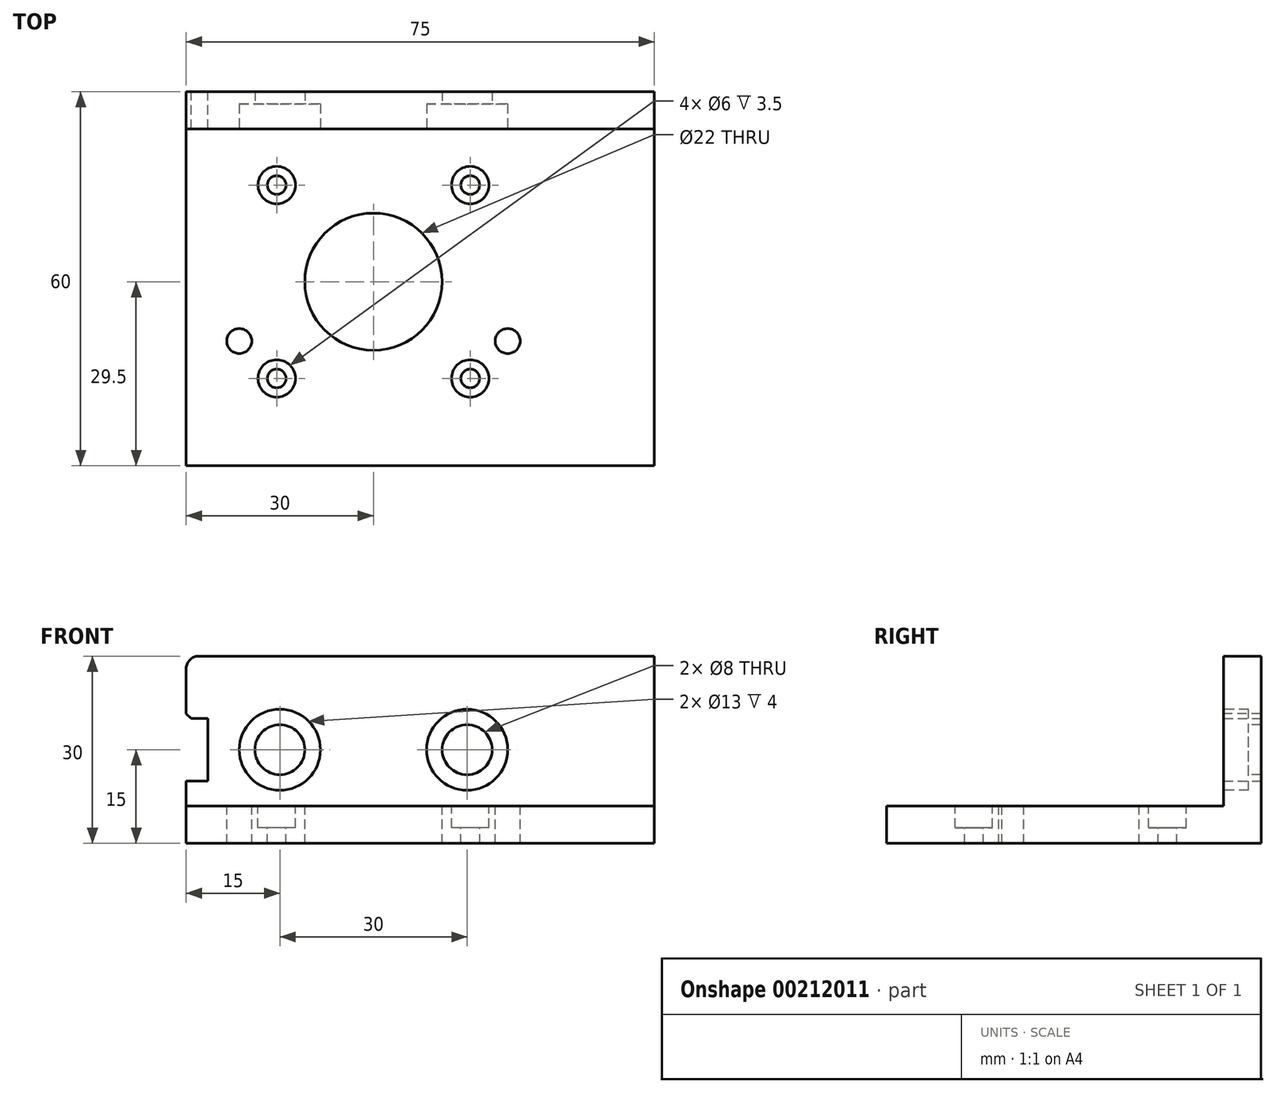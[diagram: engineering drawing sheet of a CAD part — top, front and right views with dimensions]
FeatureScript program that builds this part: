
annotation { "Feature Type Name" : "Feature", "Feature Type Description" : "" }
export const myFeature = defineFeature(function(context is Context, id is Id, definition is map)
    precondition{}
    {
        {
            var Q0;
            Q0=qCreatedBy(makeId("Top.planeOp"),FACE);
            var sketch = newSketch(context, id + "F0", { "sketchPlane" : qUnion([Q0])});
            skLineSegment(sketch, "E0.bottom", {"start": v(37.5, 30) * mm, "end": v(-37.5, 30) * mm});
            skLineSegment(sketch, "E0.top", {"start": v(37.5, -30) * mm, "end": v(-37.5, -30) * mm});
            skLineSegment(sketch, "E0.left", {"start": v(37.5, 30) * mm, "end": v(37.5, -30) * mm});
            skLineSegment(sketch, "E0.right", {"start": v(-37.5, 30) * mm, "end": v(-37.5, -30) * mm});
            skPoint(sketch, "E0.middle", {"position": v(0, 0) * mm});
            skSolve(sketch);
        }
        {
            var Q0;
            Q0 = qSketchRegion(id + "F0", true);
            extrude(context, id + "F1", {"entities" : qUnion([Q0]), "depth" : 6 * mm});
        }
        {
            var Q0;
            Q0=makeQuery(id+"F1.opExtrude","CAP_FACE",FACE,{"disambiguationData":[OSD([sQuery(id+"F0.wireOp",EDGE,"E0.bottom"),sQuery(id+"F0.wireOp",EDGE,"E0.top"),sQuery(id+"F0.wireOp",EDGE,"E0.left"),sQuery(id+"F0.wireOp",EDGE,"E0.right")])],"isStart":false});
            var sketch = newSketch(context, id + "F2", { "sketchPlane" : qUnion([Q0])});
            skLineSegment(sketch, "E1.bottom", {"start": v(-37.5, 30) * mm, "end": v(37.5, 30) * mm});
            skLineSegment(sketch, "E1.top", {"start": v(-37.5, 24) * mm, "end": v(37.5, 24) * mm});
            skLineSegment(sketch, "E1.left", {"start": v(-37.5, 30) * mm, "end": v(-37.5, 24) * mm});
            skLineSegment(sketch, "E1.right", {"start": v(37.5, 30) * mm, "end": v(37.5, 24) * mm});
            skSolve(sketch);
        }
        {
            var Q0;
            Q0 = qSketchRegion(id + "F2", true);
            extrude(context, id + "F3", {"entities" : qUnion([Q0]), "operationType" : NewBodyOperationType.ADD, "depth" : (30 - 6) * mm});
        }
        {
            var Q0;
            Q0=makeQuery(id+"F1.opExtrude","CAP_FACE",FACE,{"disambiguationData":[OSD([sQuery(id+"F0.wireOp",EDGE,"E0.bottom"),sQuery(id+"F0.wireOp",EDGE,"E0.top"),sQuery(id+"F0.wireOp",EDGE,"E0.left"),sQuery(id+"F0.wireOp",EDGE,"E0.right")])],"isStart":false});
            var sketch = newSketch(context, id + "F4", { "sketchPlane" : qUnion([Q0])});
            skCircle(sketch, "E2", {"center": v(-7.5, -0.5) * mm, "radius": 11 * mm});
            skCircle(sketch, "E3", {"center": v(-23, -16) * mm, "radius": 3 * mm});
            skCircle(sketch, "E4", {"center": v(-23, 15) * mm, "radius": 3 * mm});
            skCircle(sketch, "E5", {"center": v(8, 15) * mm, "radius": 3 * mm});
            skCircle(sketch, "E6", {"center": v(8, -16) * mm, "radius": 3 * mm});
            skCircle(sketch, "E7", {"center": v(-29, -10) * mm, "radius": 2 * mm});
            skCircle(sketch, "E8", {"center": v(14, -10) * mm, "radius": 2 * mm});
            skSolve(sketch);
        }
        {
            var Q0;
            Q0=sQuery(id+"F4.wireOp",VERTEX,"E4.center");
            var Q1;
            Q1=sQuery(id+"F4.wireOp",VERTEX,"E5.center");
            var Q2;
            Q2=sQuery(id+"F4.wireOp",VERTEX,"E6.center");
            var Q3;
            Q3=sQuery(id+"F4.wireOp",VERTEX,"E3.center");
            var Q4;
            Q4=makeQuery(id+"F1.opExtrude","SWEPT_BODY",BODY,{"disambiguationData":[OSD([sQuery(id+"F0.wireOp",EDGE,"E0.bottom"),sQuery(id+"F0.wireOp",EDGE,"E0.top"),sQuery(id+"F0.wireOp",EDGE,"E0.left"),sQuery(id+"F0.wireOp",EDGE,"E0.right")])]});
            hole(context, id + "F5", {"style" : HoleStyle.C_BORE, "endStyle" : HoleEndStyle.THROUGH, "holeDiameter" : 3 * mm, "cBoreDiameter" : 6 * mm, "cBoreDepth" : 3.5 * mm, "locations" : qUnion([Q0, Q1, Q2, Q3]), "scope" : qUnion([Q4]), "isTappedThrough" : true});
        }
        {
            var Q0;
            Q0=makeQuery(id+"F4.imprint","IMPRINT",FACE,{"disambiguationData":[TD([[makeQuery(id+"F4.imprint","IMPRINT",EDGE,{"derivedFrom":sQuery(id+"F4.wireOp",EDGE,"E2")}),1.0]])]});
            extrude(context, id + "F6", {"entities" : qUnion([Q0]), "operationType" : NewBodyOperationType.REMOVE, "endBound" : BoundingType.THROUGH_ALL, "oppositeDirection" : true, "depth" : 6.4 * mm});
        }
        {
            var Q0;
            Q0=makeQuery(id+"F4.imprint","IMPRINT",FACE,{"disambiguationData":[TD([[makeQuery(id+"F4.imprint","IMPRINT",EDGE,{"derivedFrom":sQuery(id+"F4.wireOp",EDGE,"E7")}),1.0]])]});
            var Q1;
            Q1=makeQuery(id+"F4.imprint","IMPRINT",FACE,{"disambiguationData":[TD([[makeQuery(id+"F4.imprint","IMPRINT",EDGE,{"derivedFrom":sQuery(id+"F4.wireOp",EDGE,"E8")}),1.0]])]});
            extrude(context, id + "F7", {"entities" : qUnion([Q0, Q1]), "operationType" : NewBodyOperationType.REMOVE, "endBound" : BoundingType.THROUGH_ALL, "oppositeDirection" : true, "depth" : 25 * mm});
        }
        {
            var Q0;
            Q0=makeQuery(id+"F3.opExtrude","SWEPT_FACE",FACE,{"disambiguationData":[OSD([sQuery(id+"F2.wireOp",EDGE,"E1.top")])]});
            var sketch = newSketch(context, id + "F8", { "sketchPlane" : qUnion([Q0])});
            skCircle(sketch, "E9", {"center": v(-22.5, 15) * mm, "radius": 4 * mm});
            skCircle(sketch, "E10", {"center": v(7.5, 15) * mm, "radius": 4 * mm});
            skSolve(sketch);
        }
        {
            var Q0;
            Q0=sQuery(id+"F8.wireOp",VERTEX,"E9.center");
            var Q1;
            Q1=sQuery(id+"F8.wireOp",VERTEX,"E10.center");
            var Q2;
            Q2=makeQuery(id+"F1.opExtrude","SWEPT_BODY",BODY,{"disambiguationData":[OSD([sQuery(id+"F0.wireOp",EDGE,"E0.bottom"),sQuery(id+"F0.wireOp",EDGE,"E0.top"),sQuery(id+"F0.wireOp",EDGE,"E0.left"),sQuery(id+"F0.wireOp",EDGE,"E0.right")])]});
            hole(context, id + "F9", {"style" : HoleStyle.C_BORE, "endStyle" : HoleEndStyle.THROUGH, "holeDiameter" : 8 * mm, "cBoreDiameter" : 13 * mm, "cBoreDepth" : 4 * mm, "locations" : qUnion([Q0, Q1]), "scope" : qUnion([Q2]), "isTappedThrough" : true});
        }
        {
            var Q0;
            Q0=makeQuery(id+"F3.boolean.opBoolean","MERGE",FACE,{"derivedFrom":[makeQuery(id+"F1.opExtrude","SWEPT_FACE",FACE,{"disambiguationData":[OSD([sQuery(id+"F0.wireOp",EDGE,"E0.bottom")])]}),makeQuery(id+"F3.opExtrude","SWEPT_FACE",FACE,{"disambiguationData":[OSD([sQuery(id+"F2.wireOp",EDGE,"E1.bottom")])]})]});
            var sketch = newSketch(context, id + "F10", { "sketchPlane" : qUnion([Q0])});
            skLineSegment(sketch, "E11", {"start": v(34, 10) * mm, "end": v(37.5, 10) * mm});
            skLineSegment(sketch, "E12", {"start": v(34, 10) * mm, "end": v(34, 20) * mm});
            skLineSegment(sketch, "E13", {"start": v(34, 20) * mm, "end": v(37.5, 20) * mm});
            skPoint(sketch, "E14.0", {"position": v(37.5, 15) * mm});
            skSolve(sketch);
        }
        {
            var Q0;
            {var subQ0=sQuery(id+"F10.wireOp",EDGE,"E11");Q0=makeQuery(id+"F10.imprint","IMPRINT",FACE,{"disambiguationData":[TD([[makeQuery(id+"F10.imprint","IMPRINT",EDGE,{"derivedFrom":subQ0}),1.0]])]});}
            extrude(context, id + "F11", {"entities" : qUnion([Q0]), "operationType" : NewBodyOperationType.REMOVE, "endBound" : BoundingType.THROUGH_ALL, "oppositeDirection" : true, "depth" : 25 * mm});
        }
        {
            var Q0;
            Q0=makeQuery(id+"F11.boolean.opBoolean","COPY",EDGE,{"derivedFrom":makeQuery(id+"F11.opExtrude","SWEPT_EDGE",EDGE,{"disambiguationData":[OSD([sQuery(id+"F0.wireOp",EDGE,"E0.bottom"),sQuery(id+"F0.wireOp",EDGE,"E0.right"),sQuery(id+"F2.wireOp",EDGE,"E1.bottom"),sQuery(id+"F2.wireOp",EDGE,"E1.left"),sQuery(id+"F10.wireOp",EDGE,"E13")])]})});
            var Q1;
            Q1=makeQuery(id+"F11.boolean.opBoolean","COPY",EDGE,{"derivedFrom":makeQuery(id+"F11.opExtrude","SWEPT_EDGE",EDGE,{"disambiguationData":[OSD([sQuery(id+"F0.wireOp",EDGE,"E0.bottom"),sQuery(id+"F0.wireOp",EDGE,"E0.right"),sQuery(id+"F2.wireOp",EDGE,"E1.bottom"),sQuery(id+"F2.wireOp",EDGE,"E1.left"),sQuery(id+"F10.wireOp",EDGE,"E11")])]})});
            chamfer(context, id + "F12", {"entities" : qUnion([Q0, Q1]), "width" : 0.8 * mm, "tangentPropagation" : true});
        }
        {
            var Q0;
            Q0=makeQuery(id+"F3.opExtrude","CAP_EDGE",EDGE,{"disambiguationData":[OSD([sQuery(id+"F2.wireOp",EDGE,"E1.left")])],"isStart":false});
            fillet(context, id + "F13", {"entities" : qUnion([Q0]), "radius" : 2 * mm, "tangentPropagation" : true, "allowEdgeOverflow" : false});
        }
    });
